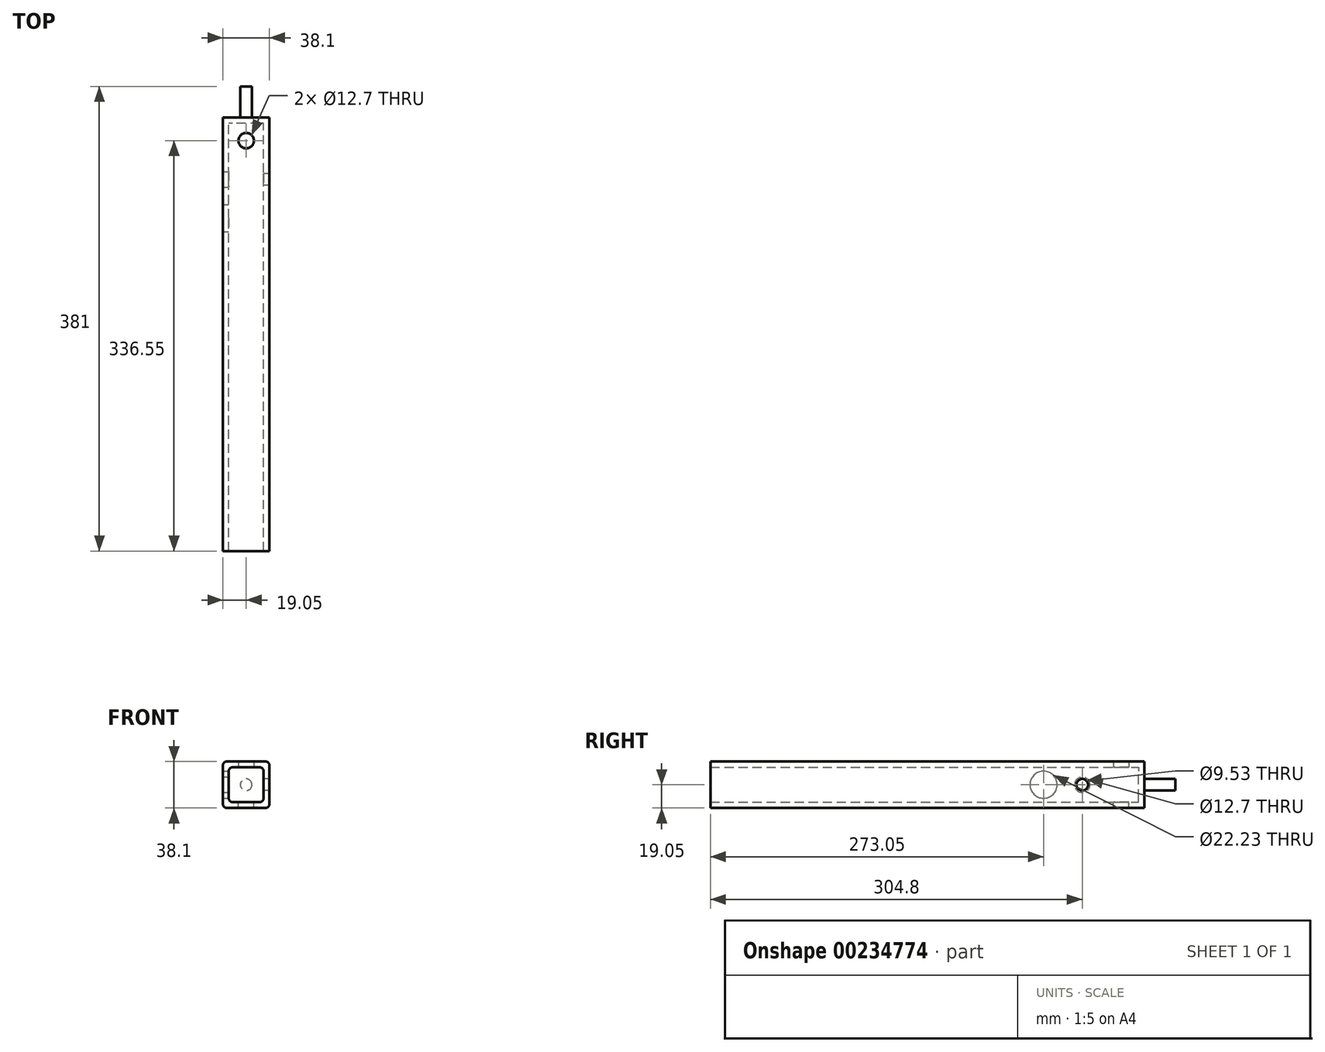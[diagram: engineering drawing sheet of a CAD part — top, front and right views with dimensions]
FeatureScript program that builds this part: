
annotation { "Feature Type Name" : "Feature", "Feature Type Description" : "" }
export const myFeature = defineFeature(function(context is Context, id is Id, definition is map)
    precondition{}
    {
        {
            var Q0;
            Q0=qCreatedBy(makeId("Front.planeOp"),FACE);
            var sketch = newSketch(context, id + "F0", { "sketchPlane" : qUnion([Q0])});
            skLineSegment(sketch, "E0.bottom", {"start": v(15.88, -19.05) * mm, "end": v(-15.88, -19.05) * mm});
            skLineSegment(sketch, "E0.top", {"start": v(15.88, 19.05) * mm, "end": v(-15.88, 19.05) * mm});
            skLineSegment(sketch, "E0.left", {"start": v(19.05, -15.88) * mm, "end": v(19.05, 15.88) * mm});
            skLineSegment(sketch, "E0.right", {"start": v(-19.05, -15.88) * mm, "end": v(-19.05, 15.87) * mm});
            skPoint(sketch, "E0.middle", {"position": v(0, 0) * mm});
            skLineSegment(sketch, "E1.bottom", {"start": v(11.11, -14.29) * mm, "end": v(-11.11, -14.29) * mm});
            skLineSegment(sketch, "E1.top", {"start": v(11.11, 14.29) * mm, "end": v(-11.11, 14.29) * mm});
            skLineSegment(sketch, "E1.left", {"start": v(14.29, -11.11) * mm, "end": v(14.29, 11.11) * mm});
            skLineSegment(sketch, "E1.right", {"start": v(-14.29, -11.11) * mm, "end": v(-14.29, 11.11) * mm});
            skPoint(sketch, "E2.visualSharp", {"position": v(-19.05, 19.05) * mm});
            skArc(sketch, "E2.filletArc", {"start": v(-15.88, 19.05) * mm, "mid": v(-18.12, 18.12) * mm, "end": v(-19.05, 15.87) * mm});
            skPoint(sketch, "E3.visualSharp", {"position": v(19.05, 19.05) * mm});
            skArc(sketch, "E3.filletArc", {"start": v(19.05, 15.88) * mm, "mid": v(18.12, 18.12) * mm, "end": v(15.88, 19.05) * mm});
            skPoint(sketch, "E4.visualSharp", {"position": v(14.29, 14.29) * mm});
            skArc(sketch, "E4.filletArc", {"start": v(14.29, 11.11) * mm, "mid": v(13.36, 13.36) * mm, "end": v(11.11, 14.29) * mm});
            skPoint(sketch, "E5.visualSharp", {"position": v(-14.29, 14.29) * mm});
            skArc(sketch, "E5.filletArc", {"start": v(-11.11, 14.29) * mm, "mid": v(-13.36, 13.36) * mm, "end": v(-14.29, 11.11) * mm});
            skPoint(sketch, "E6.visualSharp", {"position": v(-14.29, -14.29) * mm});
            skArc(sketch, "E6.filletArc", {"start": v(-14.29, -11.11) * mm, "mid": v(-13.36, -13.36) * mm, "end": v(-11.11, -14.29) * mm});
            skPoint(sketch, "E7.visualSharp", {"position": v(-19.05, -19.05) * mm});
            skArc(sketch, "E7.filletArc", {"start": v(-19.05, -15.88) * mm, "mid": v(-18.12, -18.12) * mm, "end": v(-15.88, -19.05) * mm});
            skPoint(sketch, "E8.visualSharp", {"position": v(14.29, -14.29) * mm});
            skArc(sketch, "E8.filletArc", {"start": v(11.11, -14.29) * mm, "mid": v(13.36, -13.36) * mm, "end": v(14.29, -11.11) * mm});
            skPoint(sketch, "E9.visualSharp", {"position": v(19.05, -19.05) * mm});
            skArc(sketch, "E9.filletArc", {"start": v(15.88, -19.05) * mm, "mid": v(18.12, -18.12) * mm, "end": v(19.05, -15.88) * mm});
            skCircle(sketch, "E10", {"center": v(0, 0) * mm, "radius": 4.76 * mm});
            skSolve(sketch);
        }
        {
            var Q0;
            Q0=makeQuery(id+"F0.imprint","IMPRINT",FACE,{"disambiguationData":[TD([[makeQuery(id+"F0.imprint","IMPRINT",EDGE,{"derivedFrom":sQuery(id+"F0.wireOp",EDGE,"E0.bottom")}),-1.0]])]});
            extrude(context, id + "F7", {"entities" : qUnion([Q0]), "depth" : 355.6 * mm});
        }
        {
            var Q0;
            Q0=qCreatedBy(makeId("Top.planeOp"),FACE);
            var sketch = newSketch(context, id + "F1", { "sketchPlane" : qUnion([Q0])});
            skPoint(sketch, "E11", {"position": v(0, -19.05) * mm});
            skPoint(sketch, "E12", {"position": v(0, -76.2) * mm});
            skSolve(sketch);
        }
        {
            var Q0;
            Q0=sQuery(id+"F1.wireOp",VERTEX,"E11");
            var Q1;
            Q1=makeQuery(id+"F7.opExtrude","SWEPT_BODY",BODY,{"disambiguationData":[OSD([sQuery(id+"F0.wireOp",EDGE,"E0.bottom"),sQuery(id+"F0.wireOp",EDGE,"E0.top"),sQuery(id+"F0.wireOp",EDGE,"E0.left"),sQuery(id+"F0.wireOp",EDGE,"E0.right"),sQuery(id+"F0.wireOp",EDGE,"E1.bottom"),sQuery(id+"F0.wireOp",EDGE,"E1.top"),sQuery(id+"F0.wireOp",EDGE,"E1.left"),sQuery(id+"F0.wireOp",EDGE,"E1.right"),sQuery(id+"F0.wireOp",EDGE,"E2.filletArc"),sQuery(id+"F0.wireOp",EDGE,"E3.filletArc"),sQuery(id+"F0.wireOp",EDGE,"E4.filletArc"),sQuery(id+"F0.wireOp",EDGE,"E5.filletArc"),sQuery(id+"F0.wireOp",EDGE,"E6.filletArc"),sQuery(id+"F0.wireOp",EDGE,"E7.filletArc"),sQuery(id+"F0.wireOp",EDGE,"E8.filletArc"),sQuery(id+"F0.wireOp",EDGE,"E9.filletArc")])]});
            hole(context, id + "F8", {"style" : HoleStyle.SIMPLE, "endStyle" : HoleEndStyle.THROUGH, "holeDiameter" : 12.7 * mm, "locations" : qUnion([Q0]), "scope" : qUnion([Q1]), "isTappedThrough" : true});
        }
        {
            var Q0;
            Q0=sQuery(id+"F1.wireOp",VERTEX,"E11");
            var Q1;
            Q1=makeQuery(id+"F7.opExtrude","SWEPT_BODY",BODY,{"disambiguationData":[OSD([sQuery(id+"F0.wireOp",EDGE,"E0.bottom"),sQuery(id+"F0.wireOp",EDGE,"E0.top"),sQuery(id+"F0.wireOp",EDGE,"E0.left"),sQuery(id+"F0.wireOp",EDGE,"E0.right"),sQuery(id+"F0.wireOp",EDGE,"E1.bottom"),sQuery(id+"F0.wireOp",EDGE,"E1.top"),sQuery(id+"F0.wireOp",EDGE,"E1.left"),sQuery(id+"F0.wireOp",EDGE,"E1.right"),sQuery(id+"F0.wireOp",EDGE,"E2.filletArc"),sQuery(id+"F0.wireOp",EDGE,"E3.filletArc"),sQuery(id+"F0.wireOp",EDGE,"E4.filletArc"),sQuery(id+"F0.wireOp",EDGE,"E5.filletArc"),sQuery(id+"F0.wireOp",EDGE,"E6.filletArc"),sQuery(id+"F0.wireOp",EDGE,"E7.filletArc"),sQuery(id+"F0.wireOp",EDGE,"E8.filletArc"),sQuery(id+"F0.wireOp",EDGE,"E9.filletArc")])]});
            hole(context, id + "F9", {"style" : HoleStyle.SIMPLE, "endStyle" : HoleEndStyle.THROUGH, "oppositeDirection" : true, "holeDiameter" : 12.7 * mm, "locations" : qUnion([Q0]), "scope" : qUnion([Q1]), "isTappedThrough" : true});
        }
        {
            var Q0;
            Q0=makeQuery(id+"F0.imprint","IMPRINT",FACE,{"disambiguationData":[TD([[makeQuery(id+"F0.imprint","IMPRINT",EDGE,{"derivedFrom":sQuery(id+"F0.wireOp",EDGE,"E1.bottom")}),-1.0]])]});
            var Q1;
            Q1=makeQuery(id+"F0.imprint","IMPRINT",FACE,{"disambiguationData":[TD([[makeQuery(id+"F0.imprint","IMPRINT",EDGE,{"derivedFrom":sQuery(id+"F0.wireOp",EDGE,"E10")}),1.0]])]});
            extrude(context, id + "F2", {"entities" : qUnion([Q0, Q1]), "operationType" : NewBodyOperationType.ADD, "depth" : 4.76 * mm});
        }
        {
            var Q0;
            Q0=qCreatedBy(makeId("Right.planeOp"),FACE);
            var sketch = newSketch(context, id + "F3", { "sketchPlane" : qUnion([Q0])});
            skPoint(sketch, "E13", {"position": v(0, 0) * mm});
            skPoint(sketch, "E14", {"position": v(-50.8, 0) * mm});
            skPoint(sketch, "E15", {"position": v(-82.55, 0) * mm});
            skSolve(sketch);
        }
        {
            var Q0;
            Q0=sQuery(id+"F3.wireOp",VERTEX,"E14");
            var Q1;
            Q1=makeQuery(id+"F7.opExtrude","SWEPT_BODY",BODY,{"disambiguationData":[OSD([sQuery(id+"F0.wireOp",EDGE,"E0.bottom"),sQuery(id+"F0.wireOp",EDGE,"E0.top"),sQuery(id+"F0.wireOp",EDGE,"E0.left"),sQuery(id+"F0.wireOp",EDGE,"E0.right"),sQuery(id+"F0.wireOp",EDGE,"E1.bottom"),sQuery(id+"F0.wireOp",EDGE,"E1.top"),sQuery(id+"F0.wireOp",EDGE,"E1.left"),sQuery(id+"F0.wireOp",EDGE,"E1.right"),sQuery(id+"F0.wireOp",EDGE,"E2.filletArc"),sQuery(id+"F0.wireOp",EDGE,"E3.filletArc"),sQuery(id+"F0.wireOp",EDGE,"E4.filletArc"),sQuery(id+"F0.wireOp",EDGE,"E5.filletArc"),sQuery(id+"F0.wireOp",EDGE,"E6.filletArc"),sQuery(id+"F0.wireOp",EDGE,"E7.filletArc"),sQuery(id+"F0.wireOp",EDGE,"E8.filletArc"),sQuery(id+"F0.wireOp",EDGE,"E9.filletArc")])]});
            hole(context, id + "F4", {"style" : HoleStyle.SIMPLE, "endStyle" : HoleEndStyle.THROUGH, "oppositeDirection" : true, "holeDiameter" : 9.52 * mm, "locations" : qUnion([Q0]), "scope" : qUnion([Q1]), "isTappedThrough" : true});
        }
        {
            var Q0;
            Q0=sQuery(id+"F3.wireOp",VERTEX,"E14");
            var Q1;
            Q1=makeQuery(id+"F7.opExtrude","SWEPT_BODY",BODY,{"disambiguationData":[OSD([sQuery(id+"F0.wireOp",EDGE,"E0.bottom"),sQuery(id+"F0.wireOp",EDGE,"E0.top"),sQuery(id+"F0.wireOp",EDGE,"E0.left"),sQuery(id+"F0.wireOp",EDGE,"E0.right"),sQuery(id+"F0.wireOp",EDGE,"E1.bottom"),sQuery(id+"F0.wireOp",EDGE,"E1.top"),sQuery(id+"F0.wireOp",EDGE,"E1.left"),sQuery(id+"F0.wireOp",EDGE,"E1.right"),sQuery(id+"F0.wireOp",EDGE,"E2.filletArc"),sQuery(id+"F0.wireOp",EDGE,"E3.filletArc"),sQuery(id+"F0.wireOp",EDGE,"E4.filletArc"),sQuery(id+"F0.wireOp",EDGE,"E5.filletArc"),sQuery(id+"F0.wireOp",EDGE,"E6.filletArc"),sQuery(id+"F0.wireOp",EDGE,"E7.filletArc"),sQuery(id+"F0.wireOp",EDGE,"E8.filletArc"),sQuery(id+"F0.wireOp",EDGE,"E9.filletArc")])]});
            hole(context, id + "F5", {"style" : HoleStyle.SIMPLE, "endStyle" : HoleEndStyle.THROUGH, "holeDiameter" : 12.7 * mm, "locations" : qUnion([Q0]), "scope" : qUnion([Q1]), "isTappedThrough" : true});
        }
        {
            var Q0;
            Q0=sQuery(id+"F3.wireOp",VERTEX,"E15");
            var Q1;
            Q1=makeQuery(id+"F7.opExtrude","SWEPT_BODY",BODY,{"disambiguationData":[OSD([sQuery(id+"F0.wireOp",EDGE,"E0.bottom"),sQuery(id+"F0.wireOp",EDGE,"E0.top"),sQuery(id+"F0.wireOp",EDGE,"E0.left"),sQuery(id+"F0.wireOp",EDGE,"E0.right"),sQuery(id+"F0.wireOp",EDGE,"E1.bottom"),sQuery(id+"F0.wireOp",EDGE,"E1.top"),sQuery(id+"F0.wireOp",EDGE,"E1.left"),sQuery(id+"F0.wireOp",EDGE,"E1.right"),sQuery(id+"F0.wireOp",EDGE,"E2.filletArc"),sQuery(id+"F0.wireOp",EDGE,"E3.filletArc"),sQuery(id+"F0.wireOp",EDGE,"E4.filletArc"),sQuery(id+"F0.wireOp",EDGE,"E5.filletArc"),sQuery(id+"F0.wireOp",EDGE,"E6.filletArc"),sQuery(id+"F0.wireOp",EDGE,"E7.filletArc"),sQuery(id+"F0.wireOp",EDGE,"E8.filletArc"),sQuery(id+"F0.wireOp",EDGE,"E9.filletArc")])]});
            hole(context, id + "F10", {"style" : HoleStyle.SIMPLE, "endStyle" : HoleEndStyle.THROUGH, "holeDiameter" : 22.22 * mm, "locations" : qUnion([Q0]), "scope" : qUnion([Q1]), "isTappedThrough" : true});
        }
        {
            var Q0;
            Q0=makeQuery(id+"F0.imprint","IMPRINT",FACE,{"disambiguationData":[TD([[makeQuery(id+"F0.imprint","IMPRINT",EDGE,{"derivedFrom":sQuery(id+"F0.wireOp",EDGE,"E10")}),1.0]])]});
            extrude(context, id + "F6", {"entities" : qUnion([Q0]), "operationType" : NewBodyOperationType.ADD, "oppositeDirection" : true, "depth" : 25.4 * mm});
        }
    });
